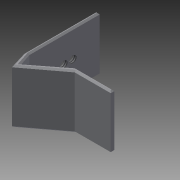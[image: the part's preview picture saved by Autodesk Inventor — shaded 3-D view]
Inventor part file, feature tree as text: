
AUTODESK INVENTOR PART (.ipt)
format: ipt  version: 2015 (Build 190159000, 159)  size: 107,008 bytes
history: native  units: in
note: dims shown in document units (in); Inventor stores cm internally (conversion verified against a paired STEP export)
features: other x3, sketch x2
ambient origin geometry x8: Origin, YZ Plane, XZ Plane, XY Plane, X Axis, Y Axis, Z Axis, Center Point
bodies: Solid1 (feature_tree)
feature tree (5):
  other  "Encoder Mount.ipt"
  other  "Solid1::Encoder Mount.ipt"
  other  "TaggingFeature1"
  sketch  "Sketch1"  dims[d0=0.3937in]
  sketch  "Sketch2"
